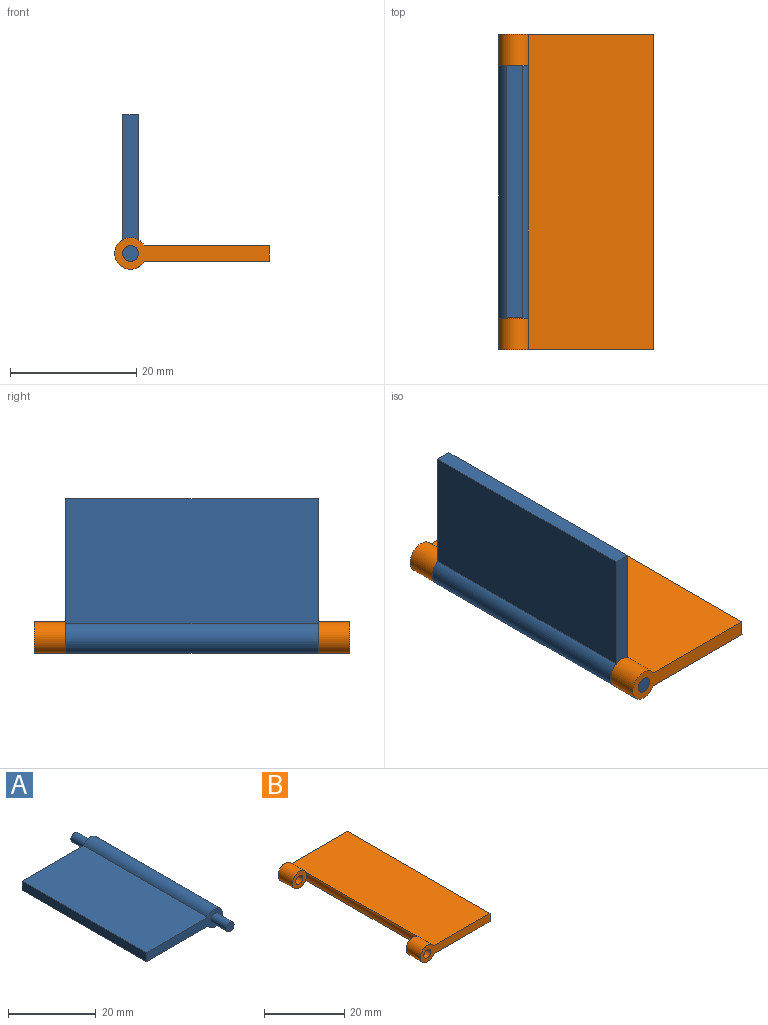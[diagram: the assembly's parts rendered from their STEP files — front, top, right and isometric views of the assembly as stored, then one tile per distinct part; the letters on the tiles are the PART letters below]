
ASSEMBLY  parts=2 mates=1
PART A: 10 faces, bbox 24.5x50x5 mm
  f0: plane 40x19.84mm, normal (0,0,1), area 793.4mm2, adj f2,f3,f4,f7
  f1: plane 40x19.84mm, normal (0,0,-1), area 793.4mm2, adj f2,f3,f4,f7
  f2: plane 40x2.5mm, normal (-1,0,0), area 100mm2, adj f0,f1,f3,f7
  f3: plane 24.5x5mm, normal (0,-1,0), area 63.7mm2, adj f0,f1,f2,f4,f5
  f4: cylinder r=2.5mm len=40mm, axis (0,1,0), area 523.6mm2, adj f0,f1,f3,f7
  f5: cylinder r=1.25mm len=5mm, axis (0,1,0), area 39.3mm2, adj f3,f6
  f6: plane 2.5x2.5mm, normal (0,-1,0), area 4.9mm2, adj f5
  f7: plane 24.5x5mm, normal (0,1,0), area 63.7mm2, adj f0,f1,f2,f4,f8
  f8: cylinder r=1.25mm len=5mm, axis (0,-1,0), area 39.3mm2, adj f7,f9
  f9: plane 2.5x2.5mm, normal (0,1,0), area 4.9mm2, adj f8
PART B: 12 faces, bbox 24.5x50x5 mm
  f0: plane 50x19.84mm, normal (0,0,1), area 991.7mm2, adj f2,f3,f4,f7,f8,f9
  f1: plane 50x19.84mm, normal (0,0,-1), area 991.7mm2, adj f2,f3,f4,f7,f8,f9
  f2: plane 24.5x5mm, normal (0,-1,0), area 63.7mm2, adj f0,f1,f3,f4,f6
  f3: plane 50x2.5mm, normal (1,0,0), area 125mm2, adj f0,f1,f2,f8
  f4: cylinder r=2.5mm len=5mm, axis (0,-1,0), area 65.4mm2, adj f0,f1,f2,f5
  f5: plane 5x5mm, normal (0,1,0), area 14.7mm2, adj f4,f6,f7
  f6: cylinder r=1.25mm len=5mm, axis (0,1,0), area 39.3mm2, adj f2,f5
  f7: cylinder r=2.5mm len=40mm, axis (0,-1,0), area 104.7mm2, adj f0,f1,f5,f10
  f8: plane 24.5x5mm, normal (0,1,0), area 63.7mm2, adj f0,f1,f3,f9,f11
  f9: cylinder r=2.5mm len=5mm, axis (0,1,0), area 65.4mm2, adj f0,f1,f8,f10
  f10: plane 5x5mm, normal (0,-1,0), area 14.7mm2, adj f7,f9,f11
  f11: cylinder r=1.25mm len=5mm, axis (0,-1,0), area 39.3mm2, adj f8,f10
PLACE A rot(axis=(0,1,0),90deg) t=(-33.23,0.65,-15.81)mm
PLACE B rot(axis=(0.27,-0.89,0.37),0deg) t=(-42.32,0.65,6.45)mm
MATE revolute A.f4 <-> B.f4  axis (0,1,0) through (-33.23,-21.85,6.45)mm
